# Revit family: 3000.111 & 112 DPJ 65x80
name_source: partatom
category: Plumbing Fixtures
units: mm (PartAtom-declared; Revit-internal decimal feet)

## family parameters
Always vertical = Yes
Cut with Voids When Loaded = No
OmniClass Number = 23.45.00.00
Part Type = Normal
Room Calculation Point = No
Round Connector Dimension = Use Diameter
Shared = No
Work Plane-Based = No

## types (2) — shared parameters
CW Connection = No
HW Connection = No
Manufacturer = Aquanight Industries Ltd
URL = www.aquaknight.co.nz
Vent Connection = No
Waste Connection = Yes

## per-type parameters (varying)
| type | Description | Inlet | Model | NV | V |
| DPJ 65x80v | DownPipe Junction 65x80 vented | 26 mm | 3000.111 | No | Yes |
| DPJ 65x80nv | DownPipe Junction 65x80 none-vented | 30 mm  [stored 0.0984252 ft] | 3000.112 | Yes | No |

note: [stored X ft] marks values corroborated as IEEE doubles in the binary element streams (Revit-internal decimal feet)

## geometry (parser evidence)
native form markers: Blend x2, Sweep x2
no freeform markers — native parametric forms only
